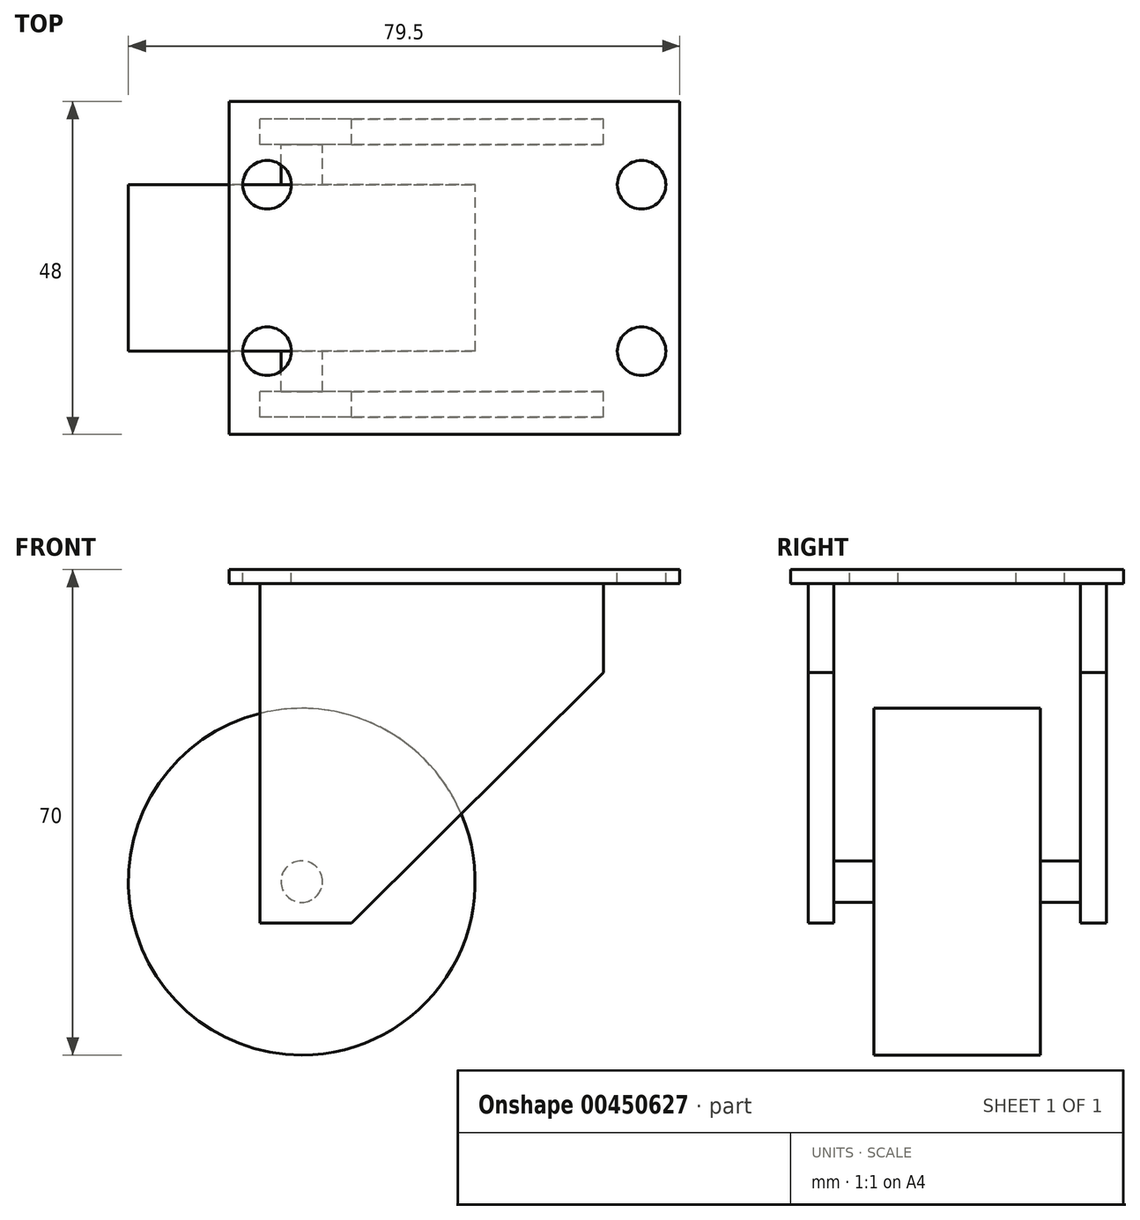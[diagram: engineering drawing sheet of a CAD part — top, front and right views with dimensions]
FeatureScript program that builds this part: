
annotation { "Feature Type Name" : "Feature", "Feature Type Description" : "" }
export const myFeature = defineFeature(function(context is Context, id is Id, definition is map)
    precondition{}
    {
        {
            var Q0;
            Q0=qCreatedBy(makeId("Top.planeOp"),FACE);
            var sketch = newSketch(context, id + "F0", { "sketchPlane" : qUnion([Q0])});
            skLineSegment(sketch, "E0.bottom", {"start": v(-32.5, 24) * mm, "end": v(32.5, 24) * mm});
            skLineSegment(sketch, "E0.top", {"start": v(-32.5, -24) * mm, "end": v(32.5, -24) * mm});
            skLineSegment(sketch, "E0.left", {"start": v(-32.5, 24) * mm, "end": v(-32.5, -24) * mm});
            skLineSegment(sketch, "E0.right", {"start": v(32.5, 24) * mm, "end": v(32.5, -24) * mm});
            skSolve(sketch);
        }
        {
            var Q0;
            Q0 = qSketchRegion(id + "F0", true);
            extrude(context, id + "F1", {"entities" : qUnion([Q0]), "depth" : 2 * mm});
        }
        {
            var Q0;
            Q0=makeQuery(id+"F1.opExtrude","CAP_FACE",FACE,{"disambiguationData":[OSD([sQuery(id+"F0.wireOp",EDGE,"E0.bottom"),sQuery(id+"F0.wireOp",EDGE,"E0.top"),sQuery(id+"F0.wireOp",EDGE,"E0.left"),sQuery(id+"F0.wireOp",EDGE,"E0.right")])],"isStart":true});
            var sketch = newSketch(context, id + "F2", { "sketchPlane" : qUnion([Q0])});
            skLineSegment(sketch, "E1.bottom", {"start": v(21.5, 21.5) * mm, "end": v(-28, 21.5) * mm});
            skLineSegment(sketch, "E1.top", {"start": v(21.5, 17.8) * mm, "end": v(-28, 17.8) * mm});
            skLineSegment(sketch, "E1.left", {"start": v(21.5, 21.5) * mm, "end": v(21.5, 17.8) * mm});
            skLineSegment(sketch, "E1.right", {"start": v(-28, 21.5) * mm, "end": v(-28, 17.8) * mm});
            skPoint(sketch, "E2.oppositeSnap0", {"position": v(-28, 19.65) * mm});
            skLineSegment(sketch, "E2.bottom", {"start": v(21.5, -17.8) * mm, "end": v(-28, -17.8) * mm});
            skLineSegment(sketch, "E2.top", {"start": v(21.5, -21.5) * mm, "end": v(-28, -21.5) * mm});
            skLineSegment(sketch, "E2.left", {"start": v(21.5, -17.8) * mm, "end": v(21.5, -21.5) * mm});
            skLineSegment(sketch, "E2.right", {"start": v(-28, -17.8) * mm, "end": v(-28, -21.5) * mm});
            skSolve(sketch);
        }
        {
            var Q0;
            Q0 = qSketchRegion(id + "F2", true);
            extrude(context, id + "F3", {"entities" : qUnion([Q0]), "operationType" : NewBodyOperationType.ADD, "depth" : 49 * mm});
        }
        {
            var Q0;
            Q0=makeQuery(id+"F3.opExtrude","SWEPT_FACE",FACE,{"disambiguationData":[OSD([sQuery(id+"F2.wireOp",EDGE,"E2.top")])]});
            var sketch = newSketch(context, id + "F4", { "sketchPlane" : qUnion([Q0])});
            skLineSegment(sketch, "E3", {"start": v(-87.67, -12.83) * mm, "end": v(94.17, -12.83) * mm, "construction": true});
            skLineSegment(sketch, "E4", {"start": v(14.8, 27.48) * mm, "end": v(14.8, -90.42) * mm, "construction": true});
            skLineSegment(sketch, "E5", {"start": v(14.8, -49) * mm, "end": v(-21.5, -12.83) * mm});
            skLineSegment(sketch, "E6", {"start": v(-21.5, -49) * mm, "end": v(14.8, -49) * mm});
            skLineSegment(sketch, "E7", {"start": v(-21.5, -49) * mm, "end": v(-21.5, -12.83) * mm});
            skSolve(sketch);
        }
        {
            var Q0;
            Q0 = qSketchRegion(id + "F4", true);
            extrude(context, id + "F5", {"entities" : qUnion([Q0]), "operationType" : NewBodyOperationType.REMOVE, "oppositeDirection" : true, "depth" : 58 * mm});
        }
        {
            var Q0;
            Q0=qCreatedBy(makeId("Front.planeOp"),FACE);
            var sketch = newSketch(context, id + "F6", { "sketchPlane" : qUnion([Q0])});
            skLineSegment(sketch, "E8", {"start": v(69, -43) * mm, "end": v(-74, -43) * mm, "construction": true});
            skLineSegment(sketch, "E9", {"start": v(-22, 20.04) * mm, "end": v(-22, -79.28) * mm, "construction": true});
            skCircle(sketch, "E10", {"center": v(-22, -43) * mm, "radius": 25 * mm});
            skSolve(sketch);
        }
        {
            var Q0;
            Q0 = qSketchRegion(id + "F6", true);
            extrude(context, id + "F7", {"entities" : qUnion([Q0]), "endBound" : BoundingType.SYMMETRIC, "depth" : 24 * mm});
        }
        {
            var Q0;
            Q0=makeQuery(id+"F1.opExtrude","CAP_FACE",FACE,{"disambiguationData":[OSD([sQuery(id+"F0.wireOp",EDGE,"E0.bottom"),sQuery(id+"F0.wireOp",EDGE,"E0.top"),sQuery(id+"F0.wireOp",EDGE,"E0.left"),sQuery(id+"F0.wireOp",EDGE,"E0.right")])],"isStart":false});
            var sketch = newSketch(context, id + "F8", { "sketchPlane" : qUnion([Q0])});
            skLineSegment(sketch, "E11", {"start": v(33.1, -12) * mm, "end": v(-41.05, -12) * mm, "construction": true});
            skLineSegment(sketch, "E12", {"start": v(33.01, 12) * mm, "end": v(-43.02, 12) * mm, "construction": true});
            skLineSegment(sketch, "E13", {"start": v(27, -21.9) * mm, "end": v(27, 29.55) * mm, "construction": true});
            skLineSegment(sketch, "E14", {"start": v(-27, -24.45) * mm, "end": v(-27, 33.38) * mm, "construction": true});
            skCircle(sketch, "E15", {"center": v(27, -12) * mm, "radius": 3.5 * mm});
            skCircle(sketch, "E16", {"center": v(-27, -12) * mm, "radius": 3.5 * mm});
            skCircle(sketch, "E17", {"center": v(-27, 12) * mm, "radius": 3.5 * mm});
            skCircle(sketch, "E18", {"center": v(27, 12) * mm, "radius": 3.5 * mm});
            skSolve(sketch);
        }
        {
            var Q0;
            Q0 = qSketchRegion(id + "F8", true);
            extrude(context, id + "F9", {"entities" : qUnion([Q0]), "operationType" : NewBodyOperationType.REMOVE, "oppositeDirection" : true, "depth" : 5 * mm});
        }
        {
            var Q0;
            Q0=makeQuery(id+"F7.opExtrude","SWEPT_BODY",BODY,{"disambiguationData":[OSD([sQuery(id+"F6.wireOp",EDGE,"E10")])]});
            deleteBodies(context, id + "F10", {"entities" : qUnion([Q0])});
        }
        {
            var Q0;
            Q0=qCreatedBy(makeId("Front.planeOp"),FACE);
            var sketch = newSketch(context, id + "F11", { "sketchPlane" : qUnion([Q0])});
            skCircle(sketch, "E19", {"center": v(-22, -43) * mm, "radius": 3 * mm});
            skSolve(sketch);
        }
        {
            var Q0;
            Q0 = qSketchRegion(id + "F11", true);
            extrude(context, id + "F12", {"entities" : qUnion([Q0]), "operationType" : NewBodyOperationType.ADD, "depth" : 18 * mm, "hasSecondDirection" : true, "secondDirectionOppositeDirection" : true, "secondDirectionDepth" : 18 * mm});
        }
        {
            var Q0;
            Q0=qCreatedBy(makeId("Front.planeOp"),FACE);
            var sketch = newSketch(context, id + "F13", { "sketchPlane" : qUnion([Q0])});
            skCircle(sketch, "E20", {"center": v(-22, -43) * mm, "radius": 25 * mm});
            skSolve(sketch);
        }
        {
            var Q0;
            Q0=makeQuery(id+"F13.imprint","IMPRINT",FACE,{"disambiguationData":[TD([[makeQuery(id+"F13.imprint","IMPRINT",EDGE,{"derivedFrom":sQuery(id+"F13.wireOp",EDGE,"E20")}),1.0]])]});
            extrude(context, id + "F14", {"entities" : qUnion([Q0]), "operationType" : NewBodyOperationType.ADD, "depth" : 12 * mm, "hasSecondDirection" : true, "secondDirectionOppositeDirection" : true, "secondDirectionDepth" : 12 * mm});
        }
    });
